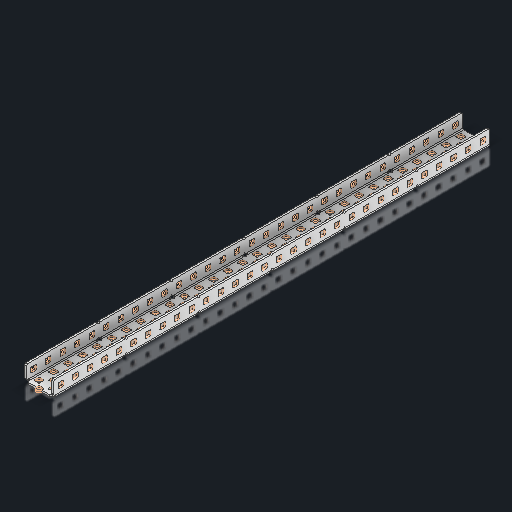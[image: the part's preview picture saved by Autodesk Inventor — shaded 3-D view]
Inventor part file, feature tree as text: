
AUTODESK INVENTOR PART (.ipt)
format: ipt  version: 2023.2 (Build 272271030, 271C)  size: 2,566,144 bytes
history: native  units: in
note: dims shown in document units (in); Inventor stores cm internally (conversion verified against a paired STEP export)
features: other x306, sketch x10, sheet_metal_op x1
ambient origin geometry x8: Origin, YZ Plane, XZ Plane, XY Plane, X Axis, Y Axis, Z Axis, Center Point
bodies: Solid1 (feature_tree)
feature tree (317):
  other  "Alu C 1x2x1x30_MIR_MIR.ipt"
  other  "Solid1::Alu C 1x2x1x30_MIR_MIR.ipt"
  other  "TaggingFeature1"
  sketch  "Sketch1"  dims[d0=0.3937in]
  sketch  "Sketch2"  dims[d1=0.0625in]
  sketch  "Sketch3"
  sketch  "Sketch7"
  other  "Flange Pattern Sketch"
  sketch  "Sketch8"
  sketch  "Sketch9"
  sheet_metal_op  "Body Pattern Sketch"
  sketch  "Sketch15"
  sketch  "Sketch16"
  other  "Arc Length"
  sketch  "Sketch13"
  sketch  "Sketch14"
  other  "Flange Pattern Plane"
  other  "Srf1"
  other  "Srf2"
  other  "Srf3"
  other  "Srf4"
  other  "Srf5"
  other  "Srf6"
  other  "Srf7"
  other  "Srf8"
  other  "Srf9"
  other  "Srf10"
  other  "Srf11"
  other  "Srf12"
  other  "Srf13"
  other  "Srf14"
  other  "Srf15"
  other  "Srf16"
  other  "Srf17"
  other  "Srf18"
  other  "Srf19"
  other  "Srf20"
  other  "Srf21"
  other  "Srf22"
  other  "Srf23"
  other  "Srf24"
  other  "Srf25"
  other  "Srf26"
  other  "Srf27"
  other  "Srf28"
  other  "Srf29"
  other  "Srf30"
  other  "Srf31"
  other  "Srf32"
  other  "Srf33"
  other  "Srf34"
  other  "Srf35"
  other  "Srf36"
  other  "Srf37"
  other  "Srf38"
  other  "Srf39"
  other  "Srf40"
  other  "Srf41"
  other  "Srf42"
  other  "Srf43"
  other  "Srf44"
  other  "Srf45"
  other  "Srf46"
  other  "Srf47"
  other  "Srf48"
  other  "Srf49"
  other  "Srf50"
  other  "Srf51"
  other  "Srf52"
  other  "Srf53"
  other  "Srf54"
  other  "Srf55"
  other  "Srf56"
  other  "Srf57"
  other  "Srf58"
  other  "Srf59"
  other  "Srf60"
  other  "Srf61"
  other  "Srf62"
  other  "Srf63"
  other  "Srf64"
  other  "Srf65"
  other  "Srf66"
  other  "Srf67"
  other  "Srf68"
  other  "Srf69"
  other  "Srf70"
  other  "Srf71"
  other  "Srf72"
  other  "Srf73"
  other  "Srf74"
  other  "Srf75"
  other  "Srf76"
  other  "Srf77"
  other  "Srf78"
  other  "Srf79"
  other  "Srf80"
  other  "Srf81"
  other  "Srf82"
  other  "Srf83"
  other  "Srf84"
  other  "Srf85"
  other  "Srf86"
  other  "Srf87"
  other  "Srf88"
  other  "Srf89"
  other  "Srf90"
  other  "Srf91"
  other  "Srf92"
  other  "Srf93"
  other  "Srf94"
  other  "Srf95"
  other  "Srf96"
  other  "Srf97"
  other  "Srf98"
  other  "Srf99"
  other  "Srf100"
  other  "Srf101"
  other  "Srf102"
  other  "Srf103"
  other  "Srf104"
  other  "Srf105"
  other  "Srf106"
  other  "Srf107"
  other  "Srf108"
  other  "Srf109"
  other  "Srf110"
  other  "Srf111"
  other  "Srf112"
  other  "Srf113"
  other  "Srf114"
  other  "Srf115"
  other  "Srf116"
  other  "Srf117"
  other  "Srf118"
  other  "Srf119"
  other  "Srf120"
  other  "Srf121"
  other  "Srf122"
  other  "Srf123"
  other  "Srf124"
  other  "Srf125"
  other  "Srf126"
  other  "Srf127"
  other  "Srf128"
  other  "Srf129"
  other  "Srf130"
  other  "Srf131"
  other  "Srf132"
  other  "Srf133"
  other  "Srf134"
  other  "Srf135"
  other  "Srf136"
  other  "Srf137"
  other  "Srf138"
  other  "Srf139"
  other  "Srf140"
  other  "Srf141"
  other  "Srf142"
  other  "Srf143"
  other  "Srf144"
  other  "Srf145"
  other  "Srf146"
  other  "Srf147"
  other  "Srf148"
  other  "Srf149"
  other  "Srf150"
  other  "Srf1::Derived"
  other  "Srf2::Derived"
  other  "Srf3::Derived"
  other  "Srf4::Derived"
  other  "Srf5::Derived"
  other  "Srf6::Derived"
  other  "Srf7::Derived"
  other  "Srf8::Derived"
  other  "Srf9::Derived"
  other  "Srf10::Derived"
  other  "Srf11::Derived"
  other  "Srf12::Derived"
  other  "Srf13::Derived"
  other  "Srf14::Derived"
  other  "Srf15::Derived"
  other  "Srf16::Derived"
  other  "Srf17::Derived"
  other  "Srf18::Derived"
  other  "Srf19::Derived"
  other  "Srf20::Derived"
  other  "Srf21::Derived"
  other  "Srf22::Derived"
  other  "Srf23::Derived"
  other  "Srf24::Derived"
  other  "Srf25::Derived"
  other  "Srf26::Derived"
  other  "Srf27::Derived"
  other  "Srf28::Derived"
  other  "Srf29::Derived"
  other  "Srf30::Derived"
  other  "Srf31::Derived"
  other  "Srf32::Derived"
  other  "Srf33::Derived"
  other  "Srf34::Derived"
  other  "Srf35::Derived"
  other  "Srf36::Derived"
  other  "Srf37::Derived"
  other  "Srf38::Derived"
  other  "Srf39::Derived"
  other  "Srf40::Derived"
  other  "Srf41::Derived"
  other  "Srf42::Derived"
  other  "Srf43::Derived"
  other  "Srf44::Derived"
  other  "Srf45::Derived"
  other  "Srf46::Derived"
  other  "Srf47::Derived"
  other  "Srf48::Derived"
  other  "Srf49::Derived"
  other  "Srf50::Derived"
  other  "Srf51::Derived"
  other  "Srf52::Derived"
  other  "Srf53::Derived"
  other  "Srf54::Derived"
  other  "Srf55::Derived"
  other  "Srf56::Derived"
  other  "Srf57::Derived"
  other  "Srf58::Derived"
  other  "Srf59::Derived"
  other  "Srf60::Derived"
  other  "Srf61::Derived"
  other  "Srf62::Derived"
  other  "Srf63::Derived"
  other  "Srf64::Derived"
  other  "Srf65::Derived"
  other  "Srf66::Derived"
  other  "Srf67::Derived"
  other  "Srf68::Derived"
  other  "Srf69::Derived"
  other  "Srf70::Derived"
  other  "Srf71::Derived"
  other  "Srf72::Derived"
  other  "Srf73::Derived"
  other  "Srf74::Derived"
  other  "Srf75::Derived"
  other  "Srf76::Derived"
  other  "Srf77::Derived"
  other  "Srf78::Derived"
  other  "Srf79::Derived"
  other  "Srf80::Derived"
  other  "Srf81::Derived"
  other  "Srf82::Derived"
  other  "Srf83::Derived"
  other  "Srf84::Derived"
  other  "Srf85::Derived"
  other  "Srf86::Derived"
  other  "Srf87::Derived"
  other  "Srf88::Derived"
  other  "Srf89::Derived"
  other  "Srf90::Derived"
  other  "Srf91::Derived"
  other  "Srf92::Derived"
  other  "Srf93::Derived"
  other  "Srf94::Derived"
  other  "Srf95::Derived"
  other  "Srf96::Derived"
  other  "Srf97::Derived"
  other  "Srf98::Derived"
  other  "Srf99::Derived"
  other  "Srf100::Derived"
  other  "Srf101::Derived"
  other  "Srf102::Derived"
  other  "Srf103::Derived"
  other  "Srf104::Derived"
  other  "Srf105::Derived"
  other  "Srf106::Derived"
  other  "Srf107::Derived"
  other  "Srf108::Derived"
  other  "Srf109::Derived"
  other  "Srf110::Derived"
  other  "Srf111::Derived"
  other  "Srf112::Derived"
  other  "Srf113::Derived"
  other  "Srf114::Derived"
  other  "Srf115::Derived"
  other  "Srf116::Derived"
  other  "Srf117::Derived"
  other  "Srf118::Derived"
  other  "Srf119::Derived"
  other  "Srf120::Derived"
  other  "Srf121::Derived"
  other  "Srf122::Derived"
  other  "Srf123::Derived"
  other  "Srf124::Derived"
  other  "Srf125::Derived"
  other  "Srf126::Derived"
  other  "Srf127::Derived"
  other  "Srf128::Derived"
  other  "Srf129::Derived"
  other  "Srf130::Derived"
  other  "Srf131::Derived"
  other  "Srf132::Derived"
  other  "Srf133::Derived"
  other  "Srf134::Derived"
  other  "Srf135::Derived"
  other  "Srf136::Derived"
  other  "Srf137::Derived"
  other  "Srf138::Derived"
  other  "Srf139::Derived"
  other  "Srf140::Derived"
  other  "Srf141::Derived"
  other  "Srf142::Derived"
  other  "Srf143::Derived"
  other  "Srf144::Derived"
  other  "Srf145::Derived"
  other  "Srf146::Derived"
  other  "Srf147::Derived"
  other  "Srf148::Derived"
  other  "Srf149::Derived"
  other  "Srf150::Derived"
